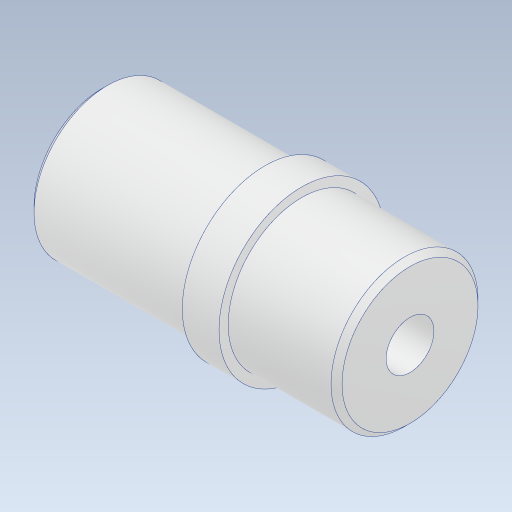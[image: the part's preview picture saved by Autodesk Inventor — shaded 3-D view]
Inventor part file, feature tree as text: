
AUTODESK INVENTOR PART (.ipt)
format: ipt  version: 2024 (Build 280153000, 153)  size: 183,296 bytes
history: native  units: mm
features: other x5, chamfer x1
ambient origin geometry x8: Origin, YZ Plane, XZ Plane, XY Plane, X Axis, Y Axis, Z Axis, Center Point
bodies: Body1 (feature_tree)
feature tree (6):
  other  "_bridseye_sketch.ipt"
  other  "厚み2"
  chamfer  "面取り1"  Distance=10.0mm
  other  "ソリッド4::_bridseye_sketch.ipt"
  other  "TaggingFeature1"
  other  "front_shoulderUnit"
